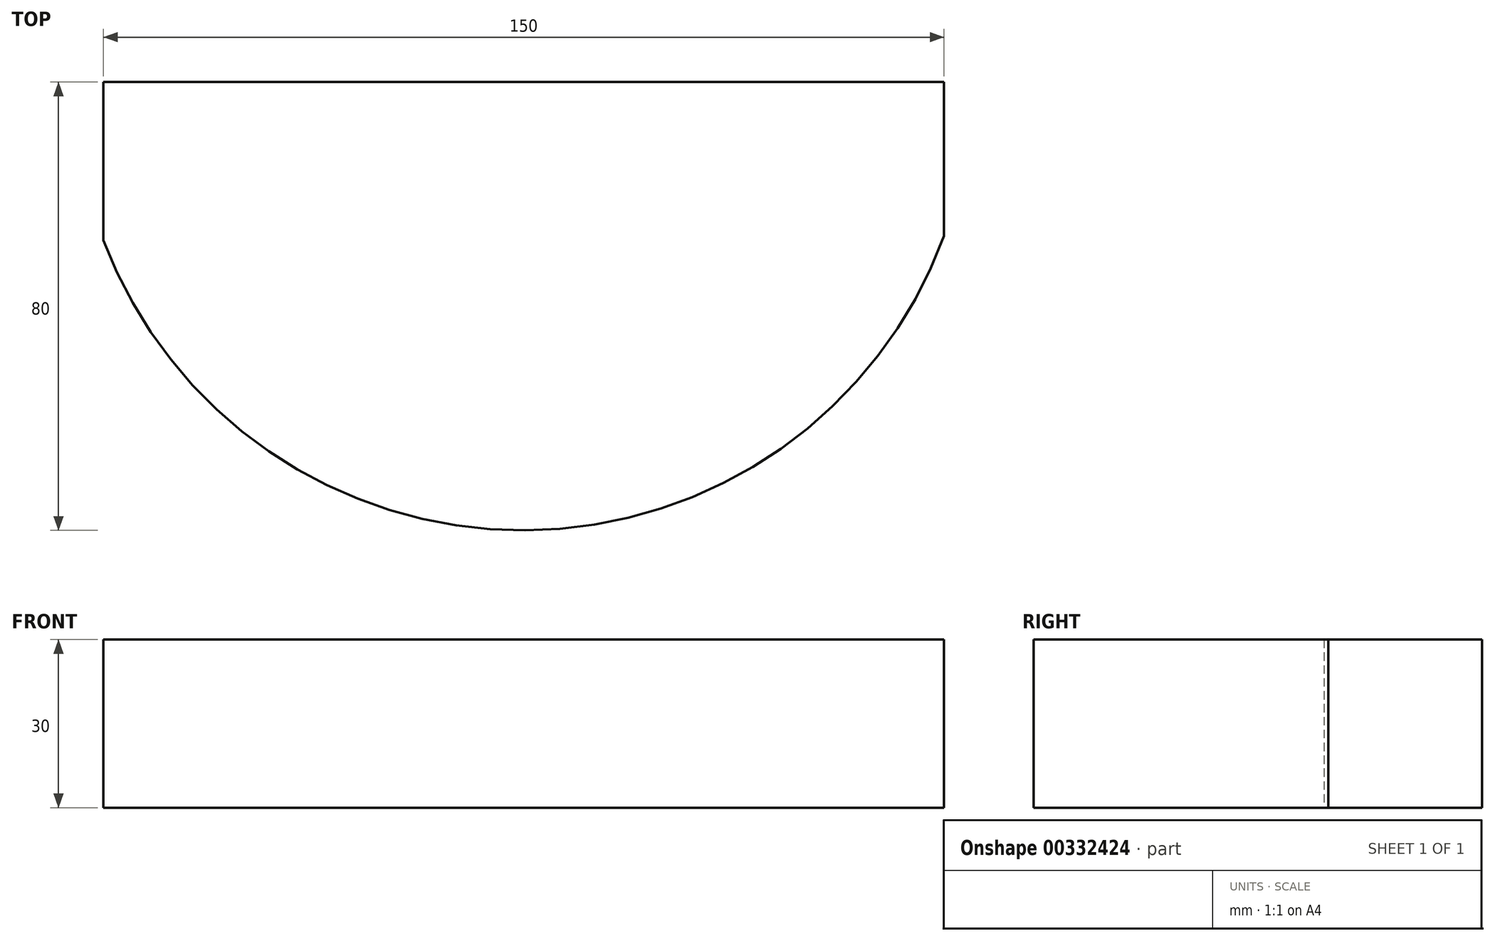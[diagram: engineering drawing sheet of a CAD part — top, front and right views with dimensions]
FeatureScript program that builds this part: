
annotation { "Feature Type Name" : "Feature", "Feature Type Description" : "" }
export const myFeature = defineFeature(function(context is Context, id is Id, definition is map)
    precondition{}
    {
        {
            var Q0;
            Q0=qCreatedBy(makeId("Top.planeOp"),FACE);
            var sketch = newSketch(context, id + "F0", { "sketchPlane" : qUnion([Q0])});
            skArc(sketch, "E0", {"start": v(-74.86, -28.22) * mm, "mid": v(0.4, -80) * mm, "end": v(75.14, -27.45) * mm});
            skLineSegment(sketch, "E1", {"start": v(-74.86, 0) * mm, "end": v(75.14, 0) * mm});
            skLineSegment(sketch, "E2", {"start": v(-74.86, 0) * mm, "end": v(-74.86, -28.22) * mm});
            skLineSegment(sketch, "E3", {"start": v(75.14, 0) * mm, "end": v(75.14, -27.45) * mm});
            skSolve(sketch);
        }
        {
            var Q0;
            Q0=makeQuery(id+"F0.imprint","IMPRINT",FACE,{"disambiguationData":[TD([[makeQuery(id+"F0.imprint","IMPRINT",EDGE,{"derivedFrom":sQuery(id+"F0.wireOp",EDGE,"E0")}),1.0]])]});
            extrude(context, id + "F1", {"entities" : qUnion([Q0]), "depth" : 30 * mm});
        }
    });
